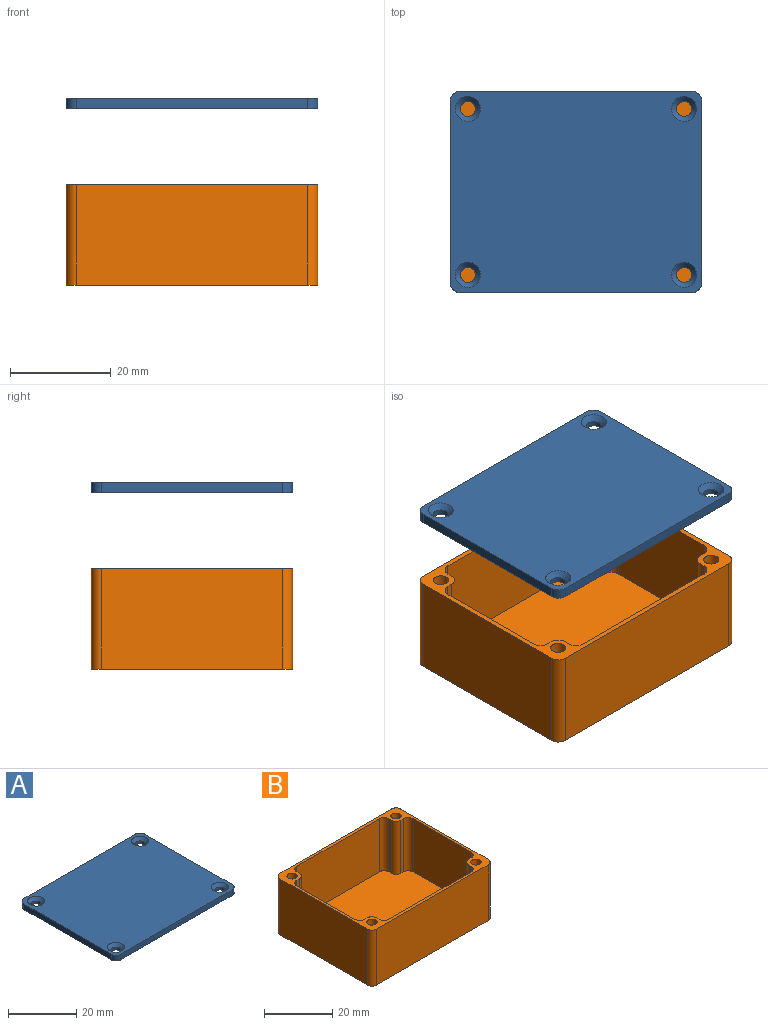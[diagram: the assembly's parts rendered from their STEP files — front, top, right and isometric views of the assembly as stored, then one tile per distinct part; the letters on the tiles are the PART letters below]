
ASSEMBLY  parts=2 mates=1
PART A: 18 faces, bbox 50x40x2 mm
  f0: plane 36x2mm, normal (-1,0,0), area 72mm2, adj f4,f5,f14,f17
  f1: plane 46x2mm, normal (0,-1,0), area 92mm2, adj f4,f5,f14,f15
  f2: plane 36x2mm, normal (1,0,0), area 72mm2, adj f4,f5,f15,f16
  f3: plane 46x2mm, normal (0,1,0), area 92mm2, adj f4,f5,f16,f17
  f4: plane 50x40mm, normal (0,0,1), area 1918mm2, adj f0,f1,f2,f3,f10,f11,f12,f13
  f5: plane 50x40mm, normal (0,0,-1), area 1968.3mm2, adj f0,f1,f2,f3,f6,f7,f8,f9
  f6: cylinder r=1.5mm len=3mm, axis (0,0,1), area 9.4mm2, adj f5,f13
  f7: cylinder r=1.5mm len=3mm, axis (0,0,1), area 9.4mm2, adj f5,f12
  f8: cylinder r=1.5mm len=3mm, axis (0,0,1), area 9.4mm2, adj f5,f11
  f9: cylinder r=1.5mm len=3mm, axis (0,0,1), area 9.4mm2, adj f5,f10
  f10: cone r=1.5mm half-angle=45deg, axis (0,0,1), area 17.8mm2, adj f4,f9
  f11: cone r=1.5mm half-angle=45deg, axis (0,0,1), area 17.8mm2, adj f4,f8
  f12: cone r=1.5mm half-angle=45deg, axis (0,0,1), area 17.8mm2, adj f4,f7
  f13: cone r=1.5mm half-angle=45deg, axis (0,0,1), area 17.8mm2, adj f4,f6
  f14: cylinder r=2mm len=2mm, axis (0,0,1), area 6.3mm2, adj f0,f1,f4,f5
  f15: cylinder r=2mm len=2mm, axis (0,0,-1), area 6.3mm2, adj f1,f2,f4,f5
  f16: cylinder r=2mm len=2mm, axis (0,0,1), area 6.3mm2, adj f2,f3,f4,f5
  f17: cylinder r=2mm len=2mm, axis (0,0,-1), area 6.3mm2, adj f0,f3,f4,f5
PART B: 43 faces, bbox 50x40x20 mm
  f0: plane 48x38mm, normal (0,0,1), area 1720.6mm2, adj f1,f2,f3,f4,f11,f12,f13,f14
  f1: plane 24x19mm, normal (1,0,0), area 456mm2, adj f0,f9,f31,f41
  f2: plane 24x19mm, normal (-1,0,0), area 456mm2, adj f0,f9,f35,f39
  f3: plane 34x19mm, normal (0,1,0), area 646mm2, adj f0,f9,f33,f36
  f4: plane 34x19mm, normal (0,-1,0), area 646mm2, adj f0,f9,f37,f42
  f5: plane 46x20mm, normal (0,1,0), area 920mm2, adj f9,f10,f27,f30
  f6: plane 36x20mm, normal (-1,0,0), area 720mm2, adj f9,f10,f27,f28
  f7: plane 46x20mm, normal (0,-1,0), area 920mm2, adj f9,f10,f28,f29
  f8: plane 36x20mm, normal (1,0,0), area 720mm2, adj f9,f10,f29,f30
  f9: plane 50x40mm, normal (0,0,1), area 247.7mm2, adj f1,f2,f3,f4,f5,f6,f7,f8
  f10: plane 50x40mm, normal (0,0,-1), area 1996.6mm2, adj f5,f6,f7,f8,f27,f28,f29,f30
  f11: plane 19x1mm, normal (1,0,0), area 19mm2, adj f0,f9,f40,f42
  f12: plane 19x1mm, normal (0,-1,0), area 19mm2, adj f0,f9,f40,f41
  f13: plane 19x1mm, normal (-1,0,0), area 19mm2, adj f0,f9,f37,f38
  f14: plane 19x1mm, normal (0,-1,0), area 19mm2, adj f0,f9,f38,f39
  f15: plane 19x1mm, normal (-1,0,0), area 19mm2, adj f0,f9,f34,f36
  f16: plane 19x1mm, normal (0,1,0), area 19mm2, adj f0,f9,f34,f35
  f17: plane 19x1mm, normal (1,0,0), area 19mm2, adj f0,f9,f32,f33
  f18: plane 19x1mm, normal (0,1,0), area 19mm2, adj f0,f9,f31,f32
  f19: cylinder r=1.5mm len=10mm, axis (0,0,1), area 94.2mm2, adj f9,f20
  f20: plane 3x3mm, normal (0,0,1), area 7.1mm2, adj f19
  f21: cylinder r=1.5mm len=10mm, axis (0,0,1), area 94.2mm2, adj f9,f22
  f22: plane 3x3mm, normal (0,0,1), area 7.1mm2, adj f21
  f23: cylinder r=1.5mm len=10mm, axis (0,0,1), area 94.2mm2, adj f9,f24
  f24: plane 3x3mm, normal (0,0,1), area 7.1mm2, adj f23
  f25: cylinder r=1.5mm len=10mm, axis (0,0,1), area 94.2mm2, adj f9,f26
  f26: plane 3x3mm, normal (0,0,1), area 7.1mm2, adj f25
  f27: cylinder r=2mm len=20mm, axis (0,0,1), area 62.8mm2, adj f5,f6,f9,f10
  f28: cylinder r=2mm len=20mm, axis (0,0,-1), area 62.8mm2, adj f6,f7,f9,f10
  f29: cylinder r=2mm len=20mm, axis (0,0,1), area 62.8mm2, adj f7,f8,f9,f10
  f30: cylinder r=2mm len=20mm, axis (0,0,-1), area 62.8mm2, adj f5,f8,f9,f10
  f31: cylinder r=2mm len=19mm, axis (0,0,1), area 59.7mm2, adj f0,f1,f9,f18
  f32: cylinder r=2mm len=19mm, axis (0,0,1), area 59.7mm2, adj f0,f9,f17,f18
  f33: cylinder r=2mm len=19mm, axis (0,0,-1), area 59.7mm2, adj f0,f3,f9,f17
  f34: cylinder r=2mm len=19mm, axis (0,0,1), area 59.7mm2, adj f0,f9,f15,f16
  f35: cylinder r=2mm len=19mm, axis (0,0,1), area 59.7mm2, adj f0,f2,f9,f16
  f36: cylinder r=2mm len=19mm, axis (0,0,1), area 59.7mm2, adj f0,f3,f9,f15
  f37: cylinder r=2mm len=19mm, axis (0,0,1), area 59.7mm2, adj f0,f4,f9,f13
  f38: cylinder r=2mm len=19mm, axis (0,0,1), area 59.7mm2, adj f0,f9,f13,f14
  f39: cylinder r=2mm len=19mm, axis (0,0,-1), area 59.7mm2, adj f0,f2,f9,f14
  f40: cylinder r=2mm len=19mm, axis (0,0,1), area 59.7mm2, adj f0,f9,f11,f12
  f41: cylinder r=2mm len=19mm, axis (0,0,-1), area 59.7mm2, adj f0,f1,f9,f12
  f42: cylinder r=2mm len=19mm, axis (0,0,-1), area 59.7mm2, adj f0,f4,f9,f11
PLACE A t=(-73.66,-34.56,52.56)mm
PLACE B t=(7.5,-35.29,17.53)mm fixed
MATE slider B.f21 <-> A.f8  axis (0,0,1) through (-8.5,-15.47,37.53)mm
